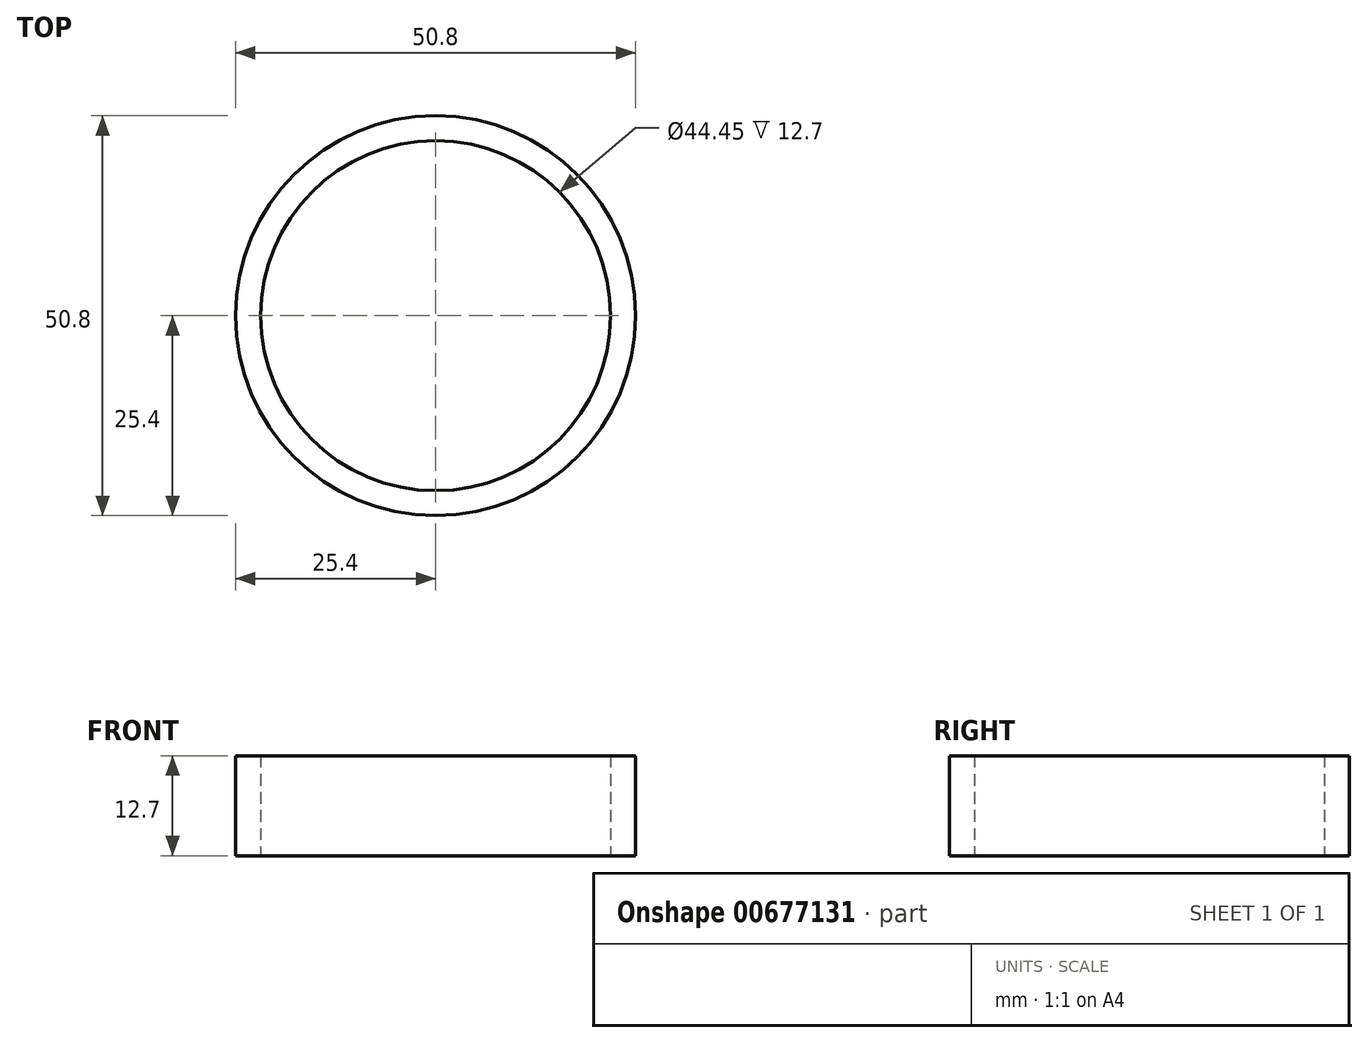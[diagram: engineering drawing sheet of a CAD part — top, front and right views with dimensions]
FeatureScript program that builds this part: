
annotation { "Feature Type Name" : "Feature", "Feature Type Description" : "" }
export const myFeature = defineFeature(function(context is Context, id is Id, definition is map)
    precondition{}
    {
        {
            var Q0;
            Q0=qCreatedBy(makeId("Top.planeOp"),FACE);
            var sketch = newSketch(context, id + "F0", { "sketchPlane" : qUnion([Q0])});
            skCircle(sketch, "E0", {"center": v(0, 0) * mm, "radius": 22.23 * mm});
            skCircle(sketch, "E1", {"center": v(0, 0) * mm, "radius": 25.4 * mm});
            skSolve(sketch);
        }
        {
            var Q0;
            Q0 = qSketchRegion(id + "F0", true);
            extrude(context, id + "F1", {"entities" : qUnion([Q0]), "depth" : 12.7 * mm, "offsetDistance" : 25.4 * mm});
        }
    });
